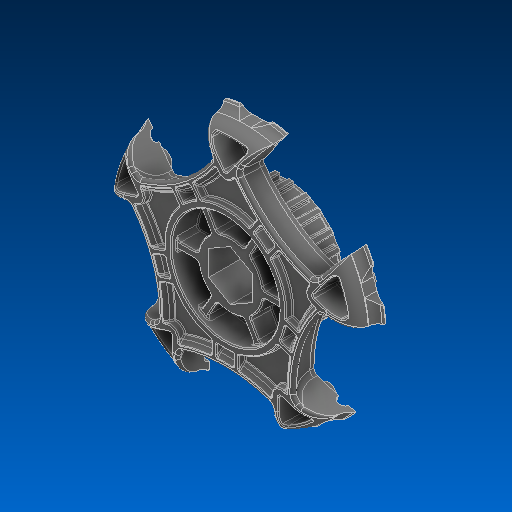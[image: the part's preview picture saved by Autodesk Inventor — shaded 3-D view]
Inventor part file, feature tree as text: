
AUTODESK INVENTOR PART (.ipt)
format: ipt  version: 2022.2 (Build 262287000, 287)  size: 3,725,312 bytes
history: native  units: in
note: dims shown in document units (in); Inventor stores cm internally (conversion verified against a paired STEP export)
features: chamfer x1
ambient origin geometry x8: Origin, YZ Plane, XZ Plane, XY Plane, X Axis, Y Axis, Z Axis, Center Point
bodies: Solid1 (feature_tree)
feature tree (1):
  chamfer  "Chamfer6"  [1 undecoded]
note: 1 required parameter value undecoded (feature->parameter linkage not recoverable at this tier; creation-order binding heuristic only, values carry confidence <= 0.55)
